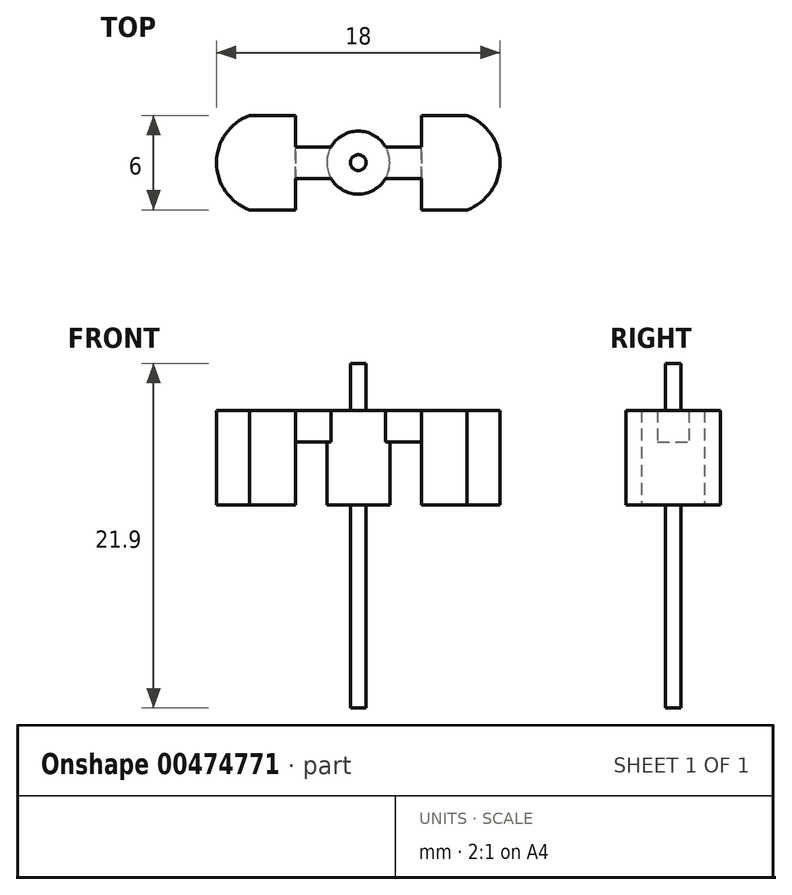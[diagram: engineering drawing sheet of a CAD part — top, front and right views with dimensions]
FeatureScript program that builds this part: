
annotation { "Feature Type Name" : "Feature", "Feature Type Description" : "" }
export const myFeature = defineFeature(function(context is Context, id is Id, definition is map)
    precondition{}
    {
        {
            var Q0;
            Q0=qCreatedBy(makeId("Top.planeOp"),FACE);
            var sketch = newSketch(context, id + "F0", { "sketchPlane" : qUnion([Q0])});
            skLineSegment(sketch, "E0", {"start": v(1.73, 1) * mm, "end": v(4, 1) * mm});
            skLineSegment(sketch, "E1", {"start": v(1.73, -1) * mm, "end": v(4, -1) * mm});
            skLineSegment(sketch, "E2", {"start": v(4, 3) * mm, "end": v(6.91, 3) * mm});
            skLineSegment(sketch, "E3", {"start": v(4, -3) * mm, "end": v(6.91, -3) * mm});
            skArc(sketch, "E4.trimOffspring", {"start": v(6.91, -3) * mm, "mid": v(9, 0) * mm, "end": v(6.91, 3) * mm});
            skLineSegment(sketch, "E5", {"start": v(4, 3) * mm, "end": v(4, 1) * mm});
            skPoint(sketch, "E6.center.orphan", {"position": v(5.78, 0) * mm});
            skArc(sketch, "E7", {"start": v(0, -2) * mm, "mid": v(1, -1.73) * mm, "end": v(1.73, -1) * mm});
            skLineSegment(sketch, "E8.trimOffspring", {"start": v(4, -1) * mm, "end": v(4, -3) * mm});
            skArc(sketch, "E9.trimOffspring", {"start": v(1.73, 1) * mm, "mid": v(1, 1.73) * mm, "end": v(0, 2) * mm});
            skLineSegment(sketch, "E10", {"start": v(6.91, 3) * mm, "end": v(6.91, -3) * mm, "construction": true});
            skArc(sketch, "E11.MirrorCS", {"start": v(-6.91, -3) * mm, "mid": v(-9, 0) * mm, "end": v(-6.91, 3) * mm});
            skLineSegment(sketch, "E12.MirrorCS", {"start": v(-1.73, -1) * mm, "end": v(-4, -1) * mm});
            skLineSegment(sketch, "E13.MirrorCS", {"start": v(-4, -3) * mm, "end": v(-6.91, -3) * mm});
            skLineSegment(sketch, "E14.MirrorCS", {"start": v(-4, 3) * mm, "end": v(-4, 1) * mm});
            skLineSegment(sketch, "E15.MirrorCS", {"start": v(-1.73, 1) * mm, "end": v(-4, 1) * mm});
            skLineSegment(sketch, "E16.MirrorCS", {"start": v(-6.91, 3) * mm, "end": v(-6.91, -3) * mm, "construction": true});
            skLineSegment(sketch, "E17.MirrorCS", {"start": v(-4, 3) * mm, "end": v(-6.91, 3) * mm});
            skPoint(sketch, "E18.MirrorP", {"position": v(-5.78, 0) * mm});
            skLineSegment(sketch, "E19.MirrorCS", {"start": v(-4, -1) * mm, "end": v(-4, -3) * mm});
            skArc(sketch, "E20.MirrorCS", {"start": v(-1.73, 1) * mm, "mid": v(-1, 1.73) * mm, "end": v(0, 2) * mm});
            skArc(sketch, "E21.MirrorCS", {"start": v(0, -2) * mm, "mid": v(-1, -1.73) * mm, "end": v(-1.73, -1) * mm});
            skSolve(sketch);
        }
        {
            var Q0;
            Q0 = qSketchRegion(id + "F0", true);
            extrude(context, id + "F1", {"entities" : qUnion([Q0]), "depth" : 6 * mm});
        }
        {
            var Q0;
            Q0=makeQuery(id+"F1.opExtrude","CAP_FACE",FACE,{"disambiguationData":[OSD([sQuery(id+"F0.wireOp",EDGE,"E0"),sQuery(id+"F0.wireOp",EDGE,"E1"),sQuery(id+"F0.wireOp",EDGE,"E2"),sQuery(id+"F0.wireOp",EDGE,"E3"),sQuery(id+"F0.wireOp",EDGE,"E4.trimOffspring"),sQuery(id+"F0.wireOp",EDGE,"E5"),sQuery(id+"F0.wireOp",EDGE,"E7"),sQuery(id+"F0.wireOp",EDGE,"E8.trimOffspring"),sQuery(id+"F0.wireOp",EDGE,"E9.trimOffspring"),sQuery(id+"F0.wireOp",EDGE,"E11.MirrorCS"),sQuery(id+"F0.wireOp",EDGE,"E12.MirrorCS"),sQuery(id+"F0.wireOp",EDGE,"E13.MirrorCS"),sQuery(id+"F0.wireOp",EDGE,"E14.MirrorCS"),sQuery(id+"F0.wireOp",EDGE,"E15.MirrorCS"),sQuery(id+"F0.wireOp",EDGE,"E17.MirrorCS"),sQuery(id+"F0.wireOp",EDGE,"E19.MirrorCS"),sQuery(id+"F0.wireOp",EDGE,"E20.MirrorCS"),sQuery(id+"F0.wireOp",EDGE,"E21.MirrorCS")])],"isStart":true});
            var sketch = newSketch(context, id + "F2", { "sketchPlane" : qUnion([Q0])});
            skArc(sketch, "E22", {"start": v(-1.73, 1) * mm, "mid": v(-2, 0) * mm, "end": v(-1.73, -1) * mm});
            skArc(sketch, "E23", {"start": v(1.73, -1) * mm, "mid": v(2, 0) * mm, "end": v(1.73, 1) * mm});
            skLineSegment(sketch, "E24", {"start": v(-4, 1) * mm, "end": v(-4, -1) * mm});
            skLineSegment(sketch, "E25", {"start": v(-4, -1) * mm, "end": v(-1.73, -1) * mm});
            skLineSegment(sketch, "E26", {"start": v(-1.73, 1) * mm, "end": v(-4, 1) * mm});
            skLineSegment(sketch, "E27", {"start": v(1.73, 1) * mm, "end": v(4, 1) * mm});
            skLineSegment(sketch, "E28", {"start": v(4, 1) * mm, "end": v(4, -1) * mm});
            skLineSegment(sketch, "E29", {"start": v(4, -1) * mm, "end": v(1.73, -1) * mm});
            skSolve(sketch);
        }
        {
            var Q0;
            Q0 = qSketchRegion(id + "F2", true);
            extrude(context, id + "F3", {"entities" : qUnion([Q0]), "operationType" : NewBodyOperationType.REMOVE, "oppositeDirection" : true, "depth" : 4 * mm});
        }
        {
            var Q0;
            Q0=makeQuery(id+"F1.opExtrude","CAP_FACE",FACE,{"disambiguationData":[OSD([sQuery(id+"F0.wireOp",EDGE,"E0"),sQuery(id+"F0.wireOp",EDGE,"E1"),sQuery(id+"F0.wireOp",EDGE,"E2"),sQuery(id+"F0.wireOp",EDGE,"E3"),sQuery(id+"F0.wireOp",EDGE,"E4.trimOffspring"),sQuery(id+"F0.wireOp",EDGE,"E5"),sQuery(id+"F0.wireOp",EDGE,"E7"),sQuery(id+"F0.wireOp",EDGE,"E8.trimOffspring"),sQuery(id+"F0.wireOp",EDGE,"E9.trimOffspring"),sQuery(id+"F0.wireOp",EDGE,"E11.MirrorCS"),sQuery(id+"F0.wireOp",EDGE,"E12.MirrorCS"),sQuery(id+"F0.wireOp",EDGE,"E13.MirrorCS"),sQuery(id+"F0.wireOp",EDGE,"E14.MirrorCS"),sQuery(id+"F0.wireOp",EDGE,"E15.MirrorCS"),sQuery(id+"F0.wireOp",EDGE,"E17.MirrorCS"),sQuery(id+"F0.wireOp",EDGE,"E19.MirrorCS"),sQuery(id+"F0.wireOp",EDGE,"E20.MirrorCS"),sQuery(id+"F0.wireOp",EDGE,"E21.MirrorCS")])],"isStart":false});
            var sketch = newSketch(context, id + "F4", { "sketchPlane" : qUnion([Q0])});
            skCircle(sketch, "E30", {"center": v(0, 0) * mm, "radius": 0.5 * mm});
            skSolve(sketch);
        }
        {
            var Q0;
            Q0 = qSketchRegion(id + "F4", true);
            extrude(context, id + "F5", {"entities" : qUnion([Q0]), "operationType" : NewBodyOperationType.ADD, "depth" : 3 * mm});
        }
        {
            var Q0;
            {var subQ0=sQuery(id+"F0.wireOp",EDGE,"E21.MirrorCS");var subQ1=sQuery(id+"F0.wireOp",EDGE,"E7");var subQ2=sQuery(id+"F0.wireOp",EDGE,"E20.MirrorCS");var subQ3=sQuery(id+"F0.wireOp",EDGE,"E9.trimOffspring");Q0=makeQuery(id+"F3.boolean.opBoolean","SPLIT",FACE,{"disambiguationData":[TD([makeQuery(id+"F3.opExtrude","SWEPT_FACE",FACE,{"disambiguationData":[OSD([sQuery(id+"F2.wireOp",EDGE,"E22")])]})])],"derivedFrom":makeQuery(id+"F1.opExtrude","CAP_FACE",FACE,{"disambiguationData":[OSD([sQuery(id+"F0.wireOp",EDGE,"E0"),sQuery(id+"F0.wireOp",EDGE,"E1"),sQuery(id+"F0.wireOp",EDGE,"E2"),sQuery(id+"F0.wireOp",EDGE,"E3"),sQuery(id+"F0.wireOp",EDGE,"E4.trimOffspring"),sQuery(id+"F0.wireOp",EDGE,"E5"),subQ1,sQuery(id+"F0.wireOp",EDGE,"E8.trimOffspring"),subQ3,sQuery(id+"F0.wireOp",EDGE,"E11.MirrorCS"),sQuery(id+"F0.wireOp",EDGE,"E12.MirrorCS"),sQuery(id+"F0.wireOp",EDGE,"E13.MirrorCS"),sQuery(id+"F0.wireOp",EDGE,"E14.MirrorCS"),sQuery(id+"F0.wireOp",EDGE,"E15.MirrorCS"),sQuery(id+"F0.wireOp",EDGE,"E17.MirrorCS"),sQuery(id+"F0.wireOp",EDGE,"E19.MirrorCS"),subQ2,subQ0])],"isStart":true})});}
            var sketch = newSketch(context, id + "F6", { "sketchPlane" : qUnion([Q0])});
            skCircle(sketch, "E31", {"center": v(0, 0) * mm, "radius": 0.5 * mm});
            skSolve(sketch);
        }
        {
            var Q0;
            Q0 = qSketchRegion(id + "F6", true);
            extrude(context, id + "F7", {"entities" : qUnion([Q0]), "operationType" : NewBodyOperationType.ADD, "depth" : 12.9 * mm});
        }
    });
